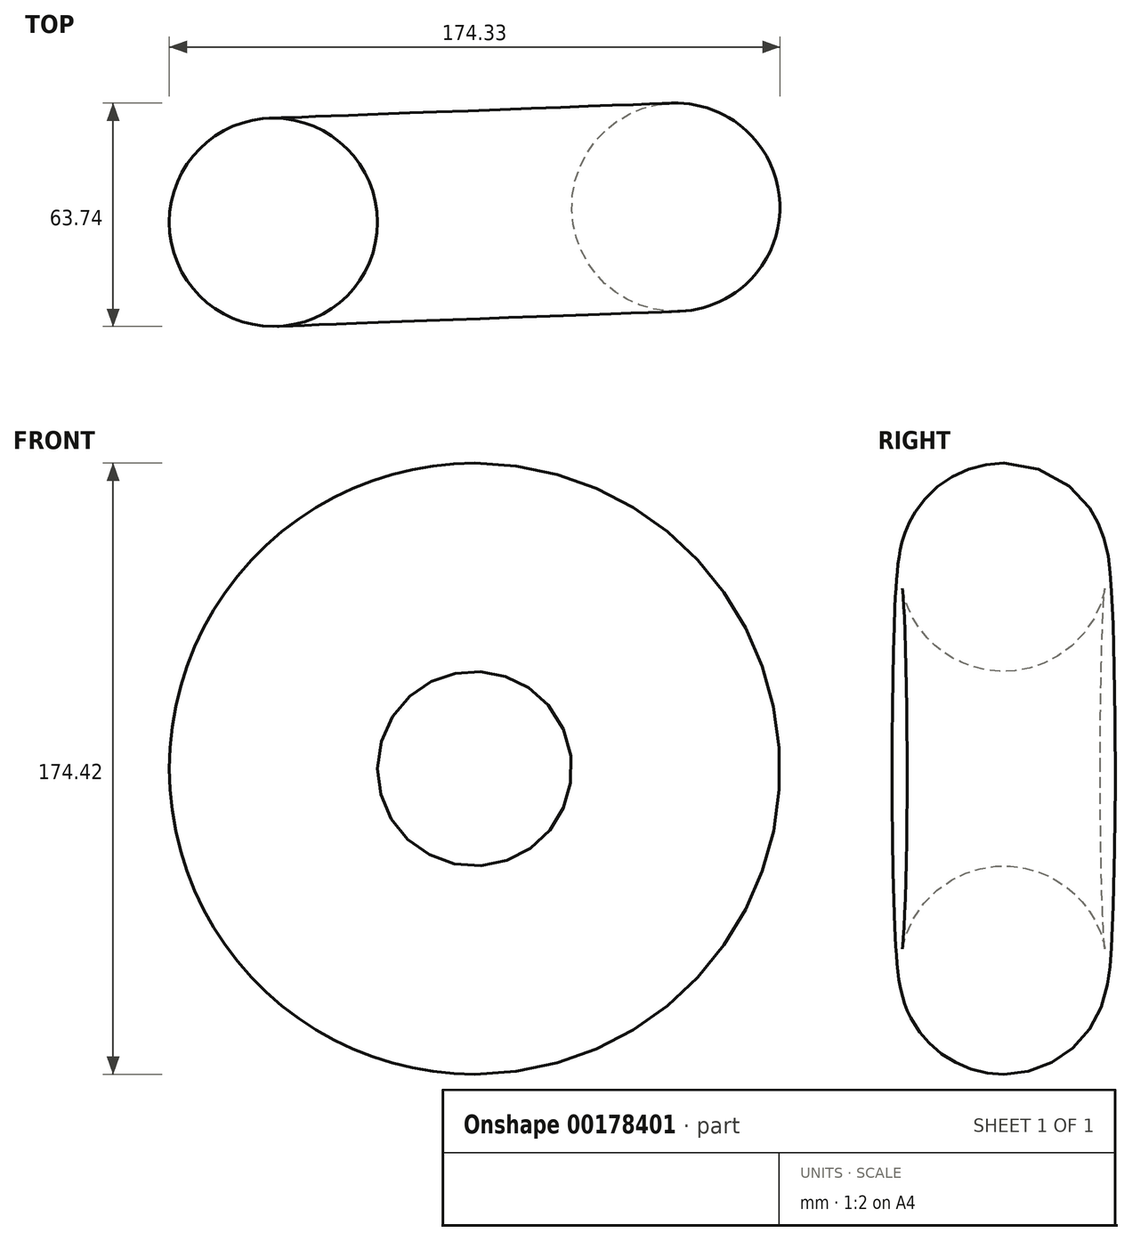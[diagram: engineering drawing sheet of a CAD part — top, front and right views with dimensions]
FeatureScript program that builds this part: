
annotation { "Feature Type Name" : "Feature", "Feature Type Description" : "" }
export const myFeature = defineFeature(function(context is Context, id is Id, definition is map)
    precondition{}
    {
        {
            var Q0;
            Q0=qCreatedBy(makeId("Top.planeOp"),FACE);
            var sketch = newSketch(context, id + "F0", { "sketchPlane" : qUnion([Q0])});
            skLineSegment(sketch, "E0", {"start": v(-12.83, 75.04) * mm, "end": v(-7.23, -74.56) * mm});
            skCircle(sketch, "E1", {"center": v(47.5, 0) * mm, "radius": 29.72 * mm});
            skSolve(sketch);
        }
        {
            var Q0;
            Q0=makeQuery(id+"F0.imprint","IMPRINT",FACE,{"disambiguationData":[TD([[makeQuery(id+"F0.imprint","IMPRINT",EDGE,{"derivedFrom":sQuery(id+"F0.wireOp",EDGE,"E1")}),1.0]])]});
            var Q1;
            Q1=sQuery(id+"F0.wireOp",EDGE,"E0");
            revolve(context, id + "F1", {"entities" : qUnion([Q0]), "axis" : qUnion([Q1]), "revolveType" : RevolveType.FULL});
        }
    });
